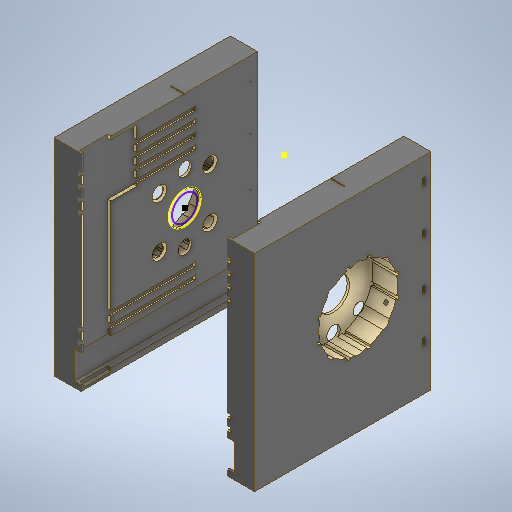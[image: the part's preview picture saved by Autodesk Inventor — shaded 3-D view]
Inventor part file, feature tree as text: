
AUTODESK INVENTOR PART (.ipt)
format: ipt  version: 2025.1 (Build 291241000, 241)  size: 2,148,352 bytes
history: native  units: mm
features: extrude x37, sketch x21, plane x2, chamfer x1, mirror x1
ambient origin geometry x8: Origin, YZ Plane, XZ Plane, XY Plane, X Axis, Y Axis, Z Axis, Center Point
bodies: Volumenkörper1 (feature_tree)
feature tree (62):
  extrude  "Extrusion1"  Depth=178.0mm
  extrude  "Extrusion2"  Depth=2.0mm
  extrude  "Extrusion3"  Depth=17.0mm
  extrude  "Extrusion4"  Depth=156.5mm TaperAngle=0.0deg
  extrude  "Extrusion5"  TaperAngle=45.0deg  [1 undecoded]
  extrude  "Extrusion6"  TaperAngle=45.0deg  [1 undecoded]
  extrude  "Extrusion7"  Depth=181.0mm TaperAngle=0.0deg
  extrude  "Extrusion8"  Depth=2.0mm TaperAngle=0.0deg
  plane  "Arbeitsebene1"
  extrude  "Extrusion9"  Depth=24.0mm
  extrude  "Extrusion10"  Depth=24.0mm
  extrude  "Extrusion11"  Depth=3.0mm TaperAngle=0.0deg
  extrude  "Extrusion12"  Depth=24.0mm
  extrude  "Extrusion13"  Depth=14.0mm
  extrude  "Extrusion14"  Depth=3.0mm TaperAngle=0.0deg
  extrude  "Extrusion15"  Depth=24.5mm
  extrude  "Extrusion16"  Depth=6.0mm
  extrude  "Extrusion17"  Depth=3.0mm TaperAngle=0.0deg
  extrude  "Extrusion20"  Depth=24.5mm
  extrude  "Extrusion21"  Depth=3.0mm
  extrude  "Extrusion22"  Depth=20.0mm
  extrude  "Extrusion23"  Depth=10.0mm
  extrude  "Extrusion24"  Depth=10.0mm
  extrude  "Extrusion25"  Depth=10.0mm
  extrude  "Extrusion26"  Depth=10.0mm
  extrude  "Extrusion27"  Depth=10.0mm
  extrude  "Extrusion28"  Depth=10.0mm
  plane  "Arbeitsebene2"
  extrude  "Extrusion29"  Depth=10.0mm
  extrude  "Extrusion30"  Depth=10.0mm
  extrude  "Extrusion31"  Depth=10.0mm
  extrude  "Extrusion32"  Depth=10.0mm
  extrude  "Extrusion33"  Depth=10.0mm
  extrude  "Extrusion34"  Depth=10.0mm
  sketch  "Skizze53"  dims[d46=6.0mm d47=6.0mm]
  extrude  "Extrusion38"  Depth=3.0mm
  chamfer  "Fasen2"  Distance=2.0mm
  extrude  "Extrusion39"  Depth=2.0mm
  extrude  "Extrusion40"  Depth=3.0mm TaperAngle=0.0deg
  extrude  "Extrusion42"  Depth=178.0mm
  extrude  "Extrusion43"  Depth=14.5mm
  mirror  "Spiegeln2"
  sketch  "Skizze3"  dims[d0=183.0mm d1=178.0mm]
  sketch  "Skizze9"  dims[d7=24.0mm d8=156.5mm d9=0.0mm]
  sketch  "Skizze10"  dims[d10=5.0mm d11=45.0deg]
  sketch  "Skizze11"  dims[d12=45.0deg d13=45.0deg]
  sketch  "Skizze12"  dims[d14=45.0deg d15=181.0mm d16=0.0mm]
  sketch  "Skizze14"  dims[d17=5.0mm d18=0.0mm d19=2.0mm d20=0.0mm]
  sketch  "Skizze30"  dims[d21=5.0mm d22=24.0mm]
  sketch  "Skizze36"  dims[d23=24.0mm d24=150.7mm]
  sketch  "Skizze45"  dims[d25=133.0mm d26=3.0mm d27=0.0mm]
  sketch  "Skizze46"  dims[d36=0.0mm d37=0.0mm d38=24.0mm]
  sketch  "Skizze47"  dims[d39=24.0mm d40=14.0mm]
  sketch  "Skizze48"  dims[d41=14.0mm d42=3.0mm d43=0.0mm]
  sketch  "Skizze49"  dims[d44=5.0mm d45=24.5mm]
  sketch  "Skizze54"  dims[d48=3.0mm d49=0.0mm d50=3.0mm d51=0.0mm]
  sketch  "Skizze - Runde Anordnung3"  dims[d2=24.0mm d3=0.0mm d4=2.0mm]
  sketch  "Skizze55"  dims[d52=2.0mm d53=24.5mm]
  sketch  "Skizze - Runde Anordnung4"  dims[d5=2.0mm d6=17.0mm]
  sketch  "Skizze56"  dims[d54=3.0mm d55=3.0mm]
  sketch  "Skizze60"  dims[d56=181.0mm d57=0.0mm d58=20.0mm]
  sketch  "Skizze61"  dims[d59=10.0mm d60=10.0mm d61=10.0mm d62=10.0mm d63=10.0mm d64=10.0mm d65=10.0mm d66=10.0mm d67=10.0mm d68=10.0mm d69=10.0mm d70=10.0mm d71=10.0mm d75=8.0mm d76=2.0mm d77=2.0mm d78=114.0mm d79=0.0mm d80=178.0mm d81=14.5mm d82=1.0mm d83=1.0mm d84=154.0mm d85=154.0mm d86=1.0mm d87=0.0mm d88=1.0mm d89=0.0mm d90=130.0mm d91=130.0mm d94=1.0mm d98=3.0mm d99=0.0mm d100=3.0mm d101=0.0mm d102=3.0mm d103=0.0mm d105=92.5mm d106=110.2mm d107=15.0mm d108=15.0mm d109=15.0mm d110=15.0mm d112=3.4mm d113=3.4mm d114=3.4mm d115=3.4mm d116=3.4mm d117=3.4mm d118=3.4mm d119=0.0mm d120=0.0mm d121=0.0mm d122=0.0mm d123=0.0mm d125=0.0mm d126=0.0mm d127=0.0mm d128=0.0mm d129=0.0mm d130=0.0mm d131=3.4mm d132=120.7mm d133=103.0mm d134=2.5mm d140=24.0mm d141=24.0mm d142=24.0mm d143=24.0mm d144=24.0mm d145=24.0mm d146=24.0mm d147=5.0mm d148=0.0mm d161=5.0mm d162=5.0mm d163=5.0mm d164=5.0mm d165=5.0mm d166=5.0mm d167=5.0mm d168=5.0mm d169=14.0mm d170=14.0mm d171=14.0mm d172=14.0mm d173=14.0mm d174=14.0mm d175=14.0mm d176=14.0mm d177=3.0mm d178=0.0mm d179=20.0mm d180=2.0mm d181=2.0mm d182=1.0mm d183=0.0mm d184=20.0mm d185=0.0mm d186=130.0mm d187=14.0mm d188=6.0mm d189=6.0mm d190=6.0mm d191=6.0mm d192=6.0mm d193=6.0mm d194=6.0mm d195=6.0mm d196=20.0mm d197=0.0mm d198=24.0mm d199=0.0mm d200=24.0mm d201=0.0mm d202=12.0mm d203=0.0mm d204=3.0mm d205=0.0mm d206=-5.0mm d207=5.7mm d208=7.0mm d209=17.0mm d210=20.0mm d211=40.0mm d212=40.0mm d213=40.0mm d214=5.7mm d215=5.7mm d216=5.7mm d217=2.6mm d218=0.0mm d219=1.6mm d220=1.6mm d221=1.6mm d222=1.6mm d223=0.0mm d224=0.0mm d225=3.4mm d226=3.4mm d227=3.4mm d228=3.4mm d229=3.4mm d230=3.4mm d231=3.4mm d232=3.4mm d233=5.7mm d234=12.0mm d235=12.0mm d236=20.0mm d237=40.0mm d238=40.0mm d239=40.0mm d240=5.7mm d241=5.7mm d242=5.7mm d243=3.4mm d244=3.4mm d245=3.4mm d246=3.4mm d247=3.4mm d248=3.4mm d249=3.4mm d250=3.4mm d251=40.0mm d252=0.0mm d253=0.0mm d254=0.0mm d255=0.0mm d256=0.0mm d257=0.0mm d258=0.0mm d259=70.05mm d260=28.39mm d261=10.0mm d262=54.0mm d263=10.0mm d264=0.0mm d265=70.05mm d266=22.5mm d267=22.0mm d268=0.0mm d292=5.75mm d294=40.0mm d295=10.0mm d296=360.0deg d297=0.0mm d298=0.0mm d299=1.5mm d300=2.0mm d301=45.0deg d303=120.0mm d304=360.0deg d305=10.0mm d306=0.0mm d307=12.0mm d308=12.0mm d309=30.0mm d310=30.0mm d311=10.0mm d312=0.0mm d313=5.5mm d314=4.0mm d315=21.214477mm d316=5.5mm d317=4.0mm d318=5.5mm d319=4.0mm d320=5.5mm d321=4.0mm d322=5.5mm d323=4.0mm d324=5.5mm d325=4.0mm d326=5.5mm d327=4.0mm d328=5.5mm d329=4.0mm d330=5.5mm d331=4.0mm d332=5.5mm d333=4.0mm d334=5.5mm d335=4.0mm d336=5.5mm d337=4.0mm d338=5.5mm d339=4.0mm d341=5.5mm d342=4.0mm d347=3.0mm d348=23.0mm d349=50.0mm d350=0.0mm d351=3.0mm d352=0.0mm]
note: 2 required parameter values undecoded (feature->parameter linkage not recoverable at this tier; creation-order binding heuristic only, values carry confidence <= 0.55)
